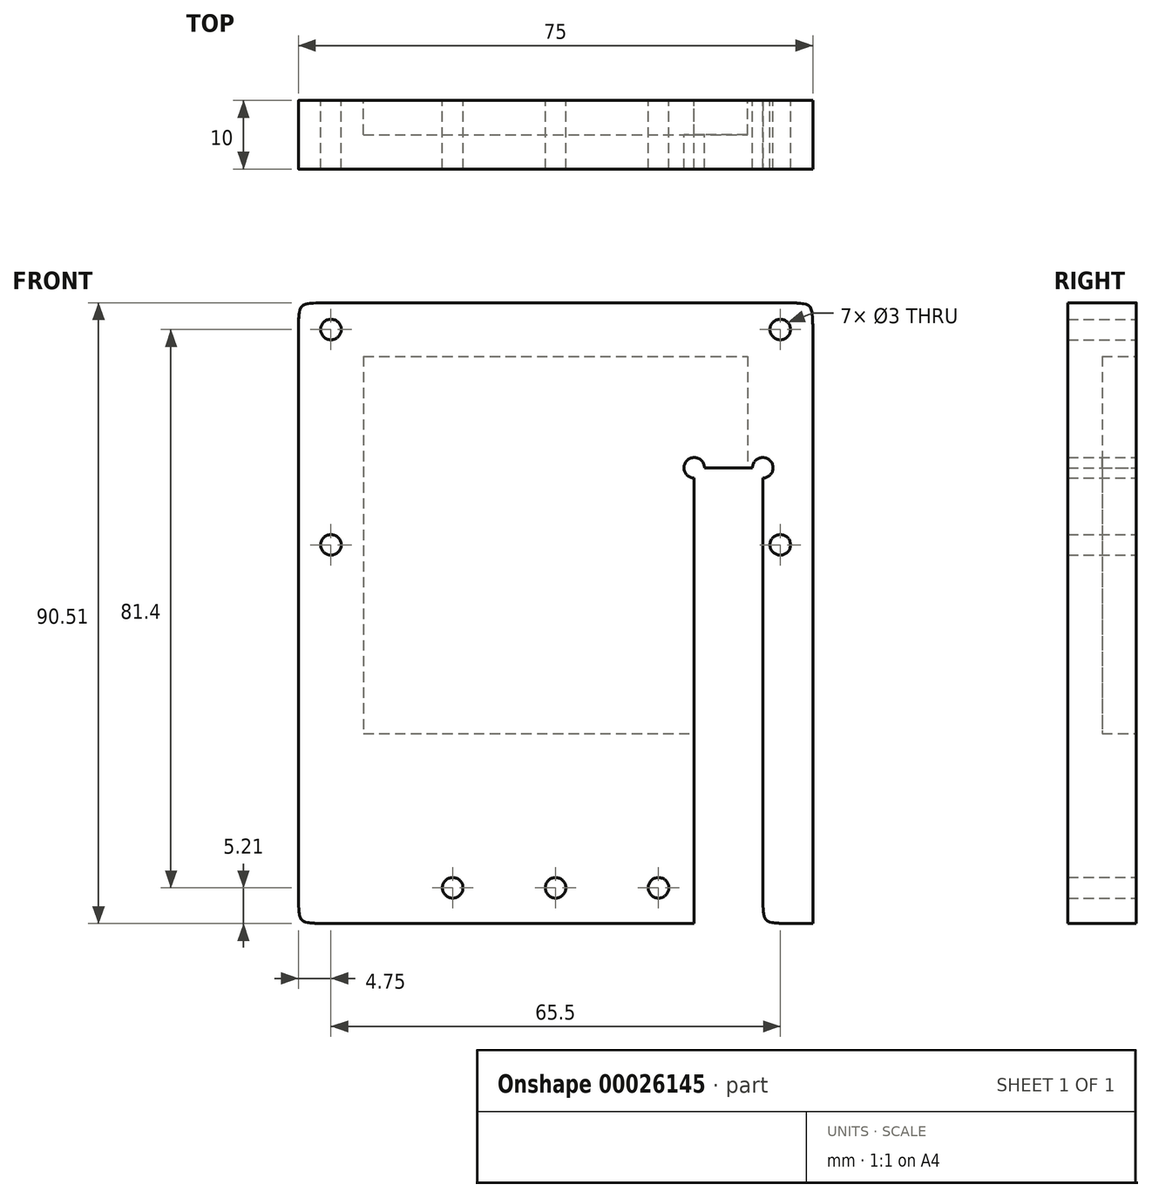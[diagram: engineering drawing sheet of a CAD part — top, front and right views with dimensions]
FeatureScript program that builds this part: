
annotation { "Feature Type Name" : "Feature", "Feature Type Description" : "" }
export const myFeature = defineFeature(function(context is Context, id is Id, definition is map)
    precondition{}
    {
        {
            var Q0;
            Q0=qCreatedBy(makeId("Front.planeOp"),FACE);
            var sketch = newSketch(context, id + "F0", { "sketchPlane" : qUnion([Q0])});
            skLineSegment(sketch, "E0.rect.top", {"start": v(37.5, 53.9) * mm, "end": v(-37.5, 53.9) * mm});
            skLineSegment(sketch, "E0.rect.right", {"start": v(-37.5, -36.61) * mm, "end": v(-37.5, 53.9) * mm});
            skPoint(sketch, "E0.rect.middle", {"position": v(0, 0) * mm});
            skLineSegment(sketch, "E1", {"start": v(-37.5, 44.37) * mm, "end": v(37.5, 44.37) * mm, "construction": true});
            skLineSegment(sketch, "E2", {"start": v(37.5, 44.37) * mm, "end": v(-37.5, -44.37) * mm, "construction": true});
            skLineSegment(sketch, "E3", {"start": v(-37.5, -44.37) * mm, "end": v(37.5, -44.37) * mm, "construction": true});
            skPoint(sketch, "E4.rect.middle", {"position": v(-19.5, 44.37) * mm});
            skPoint(sketch, "E5.rect.middle", {"position": v(19.5, 44.37) * mm});
            skPoint(sketch, "E6.rect.middle", {"position": v(-19.5, -44.37) * mm});
            skPoint(sketch, "E7.rect.middle", {"position": v(19.5, -44.37) * mm});
            skLineSegment(sketch, "E8", {"start": v(0, -25) * mm, "end": v(0, 25) * mm, "construction": true});
            skLineSegment(sketch, "E9", {"start": v(-15, 0) * mm, "end": v(15, 0) * mm, "construction": true});
            skPoint(sketch, "E10.rect.middle", {"position": v(25.15, 0) * mm});
            skPoint(sketch, "E11.orphan", {"position": v(20.1, 30.91) * mm});
            skPoint(sketch, "E10.rect.right.end.orphan", {"position": v(30.2, 30.91) * mm});
            skPoint(sketch, "E10.rect.bottom.end.orphan", {"position": v(30.2, -30.91) * mm});
            skPoint(sketch, "E10.rect.bottom.start.orphan", {"position": v(20.1, -30.91) * mm});
            skLineSegment(sketch, "E12.rect.left", {"start": v(30.2, -36.61) * mm, "end": v(30.2, -8.9) * mm});
            skPoint(sketch, "E12.rect.middle", {"position": v(25.2, -0.77) * mm});
            skPoint(sketch, "E13.center.orphan", {"position": v(20.2, -31.37) * mm});
            skPoint(sketch, "E14.center.orphan", {"position": v(30.2, -31.37) * mm});
            skPoint(sketch, "E15.orphan", {"position": v(-4.5, 40.24) * mm});
            skPoint(sketch, "E4.rect.top.start.orphan", {"position": v(-4.5, 48.5) * mm});
            skPoint(sketch, "E16.orphan", {"position": v(-34.5, 48.5) * mm});
            skPoint(sketch, "E4.rect.right.start.orphan", {"position": v(-34.5, 40.25) * mm});
            skPoint(sketch, "E5.rect.top.start.orphan", {"position": v(4.5, 48.5) * mm});
            skPoint(sketch, "E17.orphan", {"position": v(4.5, 40.24) * mm});
            skPoint(sketch, "E18.orphan", {"position": v(34.5, 48.5) * mm});
            skPoint(sketch, "E5.rect.bottom.end.orphan", {"position": v(34.5, 40.24) * mm});
            skPoint(sketch, "E19.orphan", {"position": v(-4.5, -48.5) * mm});
            skPoint(sketch, "E6.rect.left.end.orphan", {"position": v(-4.5, -40.25) * mm});
            skPoint(sketch, "E20.orphan", {"position": v(-34.5, -40.25) * mm});
            skPoint(sketch, "E6.rect.right.start.orphan", {"position": v(-34.5, -48.5) * mm});
            skPoint(sketch, "E7.rect.right.end.orphan", {"position": v(4.5, -40.24) * mm});
            skPoint(sketch, "E21.trimOffspring.end.orphan", {"position": v(4.5, -48.5) * mm});
            skPoint(sketch, "E22.orphan", {"position": v(34.5, -48.5) * mm});
            skPoint(sketch, "E7.rect.top.start.orphan", {"position": v(34.5, -40.24) * mm});
            skLineSegment(sketch, "E23.rect.bottom", {"start": v(-28, 46.1) * mm, "end": v(28, 46.1) * mm});
            skLineSegment(sketch, "E23.rect.top", {"start": v(-28, -8.9) * mm, "end": v(20.2, -8.9) * mm});
            skLineSegment(sketch, "E23.rect.left", {"start": v(-28, 46.1) * mm, "end": v(-28, -8.9) * mm});
            skLineSegment(sketch, "E23.rect.right", {"start": v(28, 46.1) * mm, "end": v(28, 29.84) * mm});
            skPoint(sketch, "E23.rect.middle", {"position": v(0, 18.6) * mm});
            skPoint(sketch, "E24.center.orphan", {"position": v(20.2, 29.84) * mm});
            skPoint(sketch, "E25.center.orphan", {"position": v(30.2, 29.84) * mm});
            skLineSegment(sketch, "E26", {"start": v(37.5, 18.6) * mm, "end": v(-37.5, 18.6) * mm, "construction": true});
            skLineSegment(sketch, "E27", {"start": v(-37.5, 18.6) * mm, "end": v(-28, 18.6) * mm, "construction": true});
            skCircle(sketch, "E28", {"center": v(-32.75, 18.6) * mm, "radius": 1.5 * mm});
            skCircle(sketch, "E29.MirrorC", {"center": v(32.75, 18.6) * mm, "radius": 1.5 * mm});
            skLineSegment(sketch, "E30", {"start": v(-28, -8.9) * mm, "end": v(28, -53.9) * mm, "construction": true});
            skCircle(sketch, "E31", {"center": v(0, -31.4) * mm, "radius": 1.5 * mm});
            skLineSegment(sketch, "E32", {"start": v(30.2, -8.9) * mm, "end": v(30.2, 28.34) * mm});
            skLineSegment(sketch, "E33", {"start": v(28.7, 29.84) * mm, "end": v(21.7, 29.84) * mm});
            skLineSegment(sketch, "E34", {"start": v(20.2, 28.34) * mm, "end": v(20.2, -8.9) * mm});
            skArc(sketch, "E35", {"start": v(30.2, 28.34) * mm, "mid": v(31.26, 30.9) * mm, "end": v(28.7, 29.84) * mm});
            skArc(sketch, "E36", {"start": v(21.7, 29.84) * mm, "mid": v(19.14, 30.9) * mm, "end": v(20.2, 28.34) * mm});
            skPoint(sketch, "E37.start.orphan", {"position": v(28, -8.9) * mm});
            skLineSegment(sketch, "E38", {"start": v(37.5, -36.61) * mm, "end": v(30.2, -36.61) * mm});
            skLineSegment(sketch, "E39", {"start": v(37.5, 53.9) * mm, "end": v(28, 46.1) * mm, "construction": true});
            skLineSegment(sketch, "E40", {"start": v(-37.5, 53.9) * mm, "end": v(-28, 46.1) * mm, "construction": true});
            skLineSegment(sketch, "E41", {"start": v(0, -31.4) * mm, "end": v(-37.5, -31.4) * mm, "construction": true});
            skPoint(sketch, "E42.center.orphan", {"position": v(-18.75, -31.4) * mm});
            skCircle(sketch, "E43", {"center": v(-15, -31.4) * mm, "radius": 1.5 * mm});
            skCircle(sketch, "E44.MirrorC", {"center": v(15, -31.4) * mm, "radius": 1.5 * mm});
            skCircle(sketch, "E45", {"center": v(32.75, 50) * mm, "radius": 1.5 * mm});
            skCircle(sketch, "E46", {"center": v(-32.75, 50) * mm, "radius": 1.5 * mm});
            skLineSegment(sketch, "E47", {"start": v(20.2, -36.61) * mm, "end": v(-37.5, -36.61) * mm});
            skLineSegment(sketch, "E48.trimOffspring", {"start": v(37.5, -36.61) * mm, "end": v(37.5, 53.9) * mm});
            skPoint(sketch, "E0.rect.bottom.start.orphan", {"position": v(37.5, -53.9) * mm});
            skPoint(sketch, "E49.orphan", {"position": v(30.2, -53.9) * mm});
            skLineSegment(sketch, "E50.trimOffspring", {"start": v(20.2, -36.61) * mm, "end": v(20.2, -8.9) * mm});
            skPoint(sketch, "E51.orphan", {"position": v(-37.5, -53.9) * mm});
            skSolve(sketch);
        }
        {
            var Q0;
            Q0=makeQuery(id+"F0.imprint","IMPRINT",FACE,{"disambiguationData":[TD([[makeQuery(id+"F0.imprint","IMPRINT",EDGE,{"derivedFrom":sQuery(id+"F0.wireOp",EDGE,"E23.rect.bottom")}),-1.0]])]});
            var Q1;
            {var subQ7=sQuery(id+"F0.wireOp",EDGE,"E0.rect.top");Q1=makeQuery(id+"F0.imprint","IMPRINT",FACE,{"disambiguationData":[TD([[makeQuery(id+"F0.imprint","IMPRINT",EDGE,{"derivedFrom":subQ7}),1.0]])]});}
            extrude(context, id + "F1", {"entities" : qUnion([Q0, Q1]), "depth" : 10 * mm});
        }
        {
            var Q0;
            Q0=makeQuery(id+"F1.opExtrude","SWEPT_EDGE",EDGE,{"disambiguationData":[OSD([sQuery(id+"F0.wireOp",EDGE,"E0.rect.top"),sQuery(id+"F0.wireOp",EDGE,"E0.rect.right")])]});
            var Q1;
            Q1=makeQuery(id+"F1.opExtrude","SWEPT_EDGE",EDGE,{"disambiguationData":[OSD([sQuery(id+"F0.wireOp",EDGE,"E0.rect.bottom"),sQuery(id+"F0.wireOp",EDGE,"E0.rect.right")])]});
            var Q2;
            Q2=makeQuery(id+"F1.opExtrude","SWEPT_EDGE",EDGE,{"disambiguationData":[OSD([sQuery(id+"F0.wireOp",EDGE,"E0.rect.bottom"),sQuery(id+"F0.wireOp",EDGE,"E0.rect.left")])]});
            var Q3;
            Q3=makeQuery(id+"F1.opExtrude","SWEPT_EDGE",EDGE,{"disambiguationData":[OSD([sQuery(id+"F0.wireOp",EDGE,"E0.rect.top"),sQuery(id+"F0.wireOp",EDGE,"E0.rect.left")])]});
            var Q4;
            Q4=makeQuery(id+"F1.opExtrude","SWEPT_EDGE",EDGE,{"disambiguationData":[OSD([sQuery(id+"F0.wireOp",EDGE,"427d9130-ed9a-4b5e-adfc-3cf5be296974.trimOffspring"),sQuery(id+"F0.wireOp",EDGE,"dc01f706-e9b0-4246-b6ca-897daf157666.trimOffspring")])]});
            var Q5;
            Q5=makeQuery(id+"F1.opExtrude","SWEPT_EDGE",EDGE,{"disambiguationData":[OSD([sQuery(id+"F0.wireOp",EDGE,"E12.rect.left"),sQuery(id+"F0.wireOp",EDGE,"E38")])]});
            fillet(context, id + "F2", {"entities" : qUnion([Q0, Q1, Q2, Q3, Q4, Q5]), "radius" : 5 * mm, "tangentPropagation" : true, "rho" : 0.8, "crossSection" : FilletCrossSection.CONIC, "allowEdgeOverflow" : false});
        }
        {
            var Q0;
            Q0=makeQuery(id+"F0.imprint","IMPRINT",FACE,{"disambiguationData":[TD([[makeQuery(id+"F0.imprint","IMPRINT",EDGE,{"derivedFrom":sQuery(id+"F0.wireOp",EDGE,"E23.rect.bottom")}),-1.0]])]});
            extrude(context, id + "F3", {"entities" : qUnion([Q0]), "operationType" : NewBodyOperationType.REMOVE, "depth" : 5 * mm});
        }
    });
